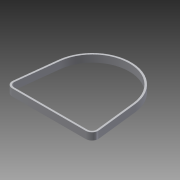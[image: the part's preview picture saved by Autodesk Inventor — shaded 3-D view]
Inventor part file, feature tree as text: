
AUTODESK INVENTOR PART (.ipt)
format: ipt  version: 2014 SP1 (Build 180222100, 222)  size: 99,328 bytes
history: native  units: in
note: dims shown in document units (in); Inventor stores cm internally (conversion verified against a paired STEP export)
features: extrude x1, sketch x1
ambient origin geometry x8: Origin, YZ Plane, XZ Plane, XY Plane, X Axis, Y Axis, Z Axis, Center Point
bodies: Solid1 (feature_tree)
feature tree (2):
  extrude  "Extrusion1"  Depth=0.2in
  sketch  "Sketch1"  dims[d0=2.062in d1=2.062in d2=0.25in d3=0.25in d4=0.125in d5=0.05in d6=0.05in d7=0.05in d8=0.05in d9=0.2in d10=0.0in]
